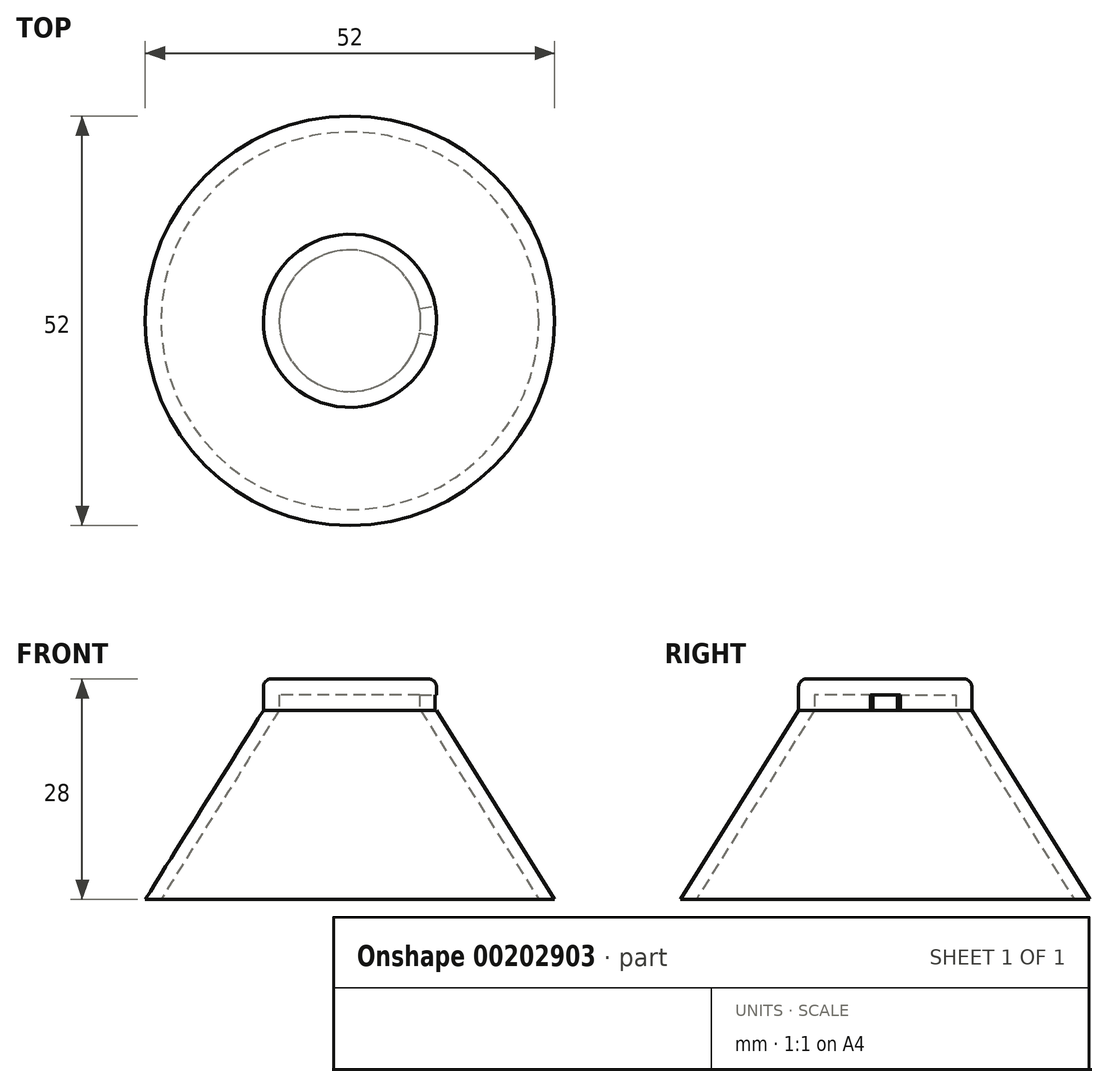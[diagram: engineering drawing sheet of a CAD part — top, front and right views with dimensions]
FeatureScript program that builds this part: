
annotation { "Feature Type Name" : "Feature", "Feature Type Description" : "" }
export const myFeature = defineFeature(function(context is Context, id is Id, definition is map)
    precondition{}
    {
        {
            var Q0;
            Q0=qCreatedBy(makeId("Front.planeOp"),FACE);
            var sketch = newSketch(context, id + "F0", { "sketchPlane" : qUnion([Q0])});
            skLineSegment(sketch, "E0", {"start": v(9, 24) * mm, "end": v(24, 0) * mm});
            skLineSegment(sketch, "E1", {"start": v(9, 24) * mm, "end": v(11, 24) * mm});
            skLineSegment(sketch, "E2", {"start": v(11, 24) * mm, "end": v(26, 0) * mm});
            skLineSegment(sketch, "E3", {"start": v(26, 0) * mm, "end": v(24, 0) * mm});
            skLineSegment(sketch, "E4", {"start": v(0, 0) * mm, "end": v(0, 24) * mm, "construction": true});
            skSolve(sketch);
        }
        {
            var Q0;
            Q0=qSketchRegion(id+"F0",true);
            var Q1;
            Q1=sQuery(id+"F0.wireOp",EDGE,"E4");
            revolve(context, id + "F1", {"entities" : qUnion([Q0]), "axis" : qUnion([Q1]), "revolveType" : RevolveType.FULL});
        }
        {
            var Q0;
            Q0=qCreatedBy(makeId("Front.planeOp"),FACE);
            var sketch = newSketch(context, id + "F2", { "sketchPlane" : qUnion([Q0])});
            skLineSegment(sketch, "E5", {"start": v(0, 0) * mm, "end": v(0, 57.6) * mm, "construction": true});
            skLineSegment(sketch, "E6", {"start": v(9, 24) * mm, "end": v(0, 38.46) * mm, "construction": true});
            skSolve(sketch);
        }
        {
            var Q0;
            Q0=makeQuery(id+"F1.opRevolve","SWEPT_FACE",FACE,{"disambiguationData":[OSD([sQuery(id+"F0.wireOp",EDGE,"E1")])]});
            extrude(context, id + "F3", {"entities" : qUnion([Q0]), "depth" : 2 * mm});
        }
        {
            var Q0;
            Q0=qCreatedBy(makeId("Front.planeOp"),FACE);
            var sketch = newSketch(context, id + "F4", { "sketchPlane" : qUnion([Q0])});
            skLineSegment(sketch, "E7.bottom", {"start": v(9, 26) * mm, "end": v(11, 26) * mm});
            skLineSegment(sketch, "E7.top", {"start": v(9, 24) * mm, "end": v(11, 24) * mm});
            skLineSegment(sketch, "E7.left", {"start": v(9, 26) * mm, "end": v(9, 24) * mm});
            skLineSegment(sketch, "E7.right", {"start": v(11, 26) * mm, "end": v(11, 24) * mm});
            skSolve(sketch);
        }
        {
            var Q0;
            {var subQ0=sQuery(id+"F0.wireOp",EDGE,"E1");var subQ3=sQuery(id+"F4.wireOp",EDGE,"E7.right");var subQ4=sQuery(id+"F4.wireOp",EDGE,"E7.left");var subQ5=sQuery(id+"F4.wireOp",EDGE,"E7.top");var subQ6=sQuery(id+"F4.wireOp",EDGE,"E7.bottom");var subQ7=makeQuery(id+"FlPVtqmiziweMUE_2.4.F7.opRevolve","CAP_FACE",FACE,{"disambiguationData":[OSD([subQ6,subQ5,subQ4,subQ3])],"isStart":true});var subQ8=makeQuery(id+"F7.boolean.opBoolean","COPY",FACE,{"derivedFrom":makeQuery(id+"F7.opRevolve","CAP_FACE",FACE,{"disambiguationData":[OSD([subQ6,subQ5,subQ4,subQ3])],"isStart":false})});Q0=makeQuery(id+"FlPVtqmiziweMUE_2.5.F7.boolean.opBoolean","SPLIT",FACE,{"disambiguationData":[TD([makeQuery(id+"FlPVtqmiziweMUE_2.4.F7.boolean.opBoolean","COPY",FACE,{"derivedFrom":subQ7})])],"derivedFrom":makeQuery(id+"FlPVtqmiziweMUE_2.4.F7.boolean.opBoolean","SPLIT",FACE,{"disambiguationData":[TD([subQ8])],"derivedFrom":makeQuery(id+"FlPVtqmiziweMUE_2.3.F7.boolean.opBoolean","SPLIT",FACE,{"disambiguationData":[TD([subQ8])],"derivedFrom":makeQuery(id+"FlPVtqmiziweMUE_2.2.F7.boolean.opBoolean","SPLIT",FACE,{"disambiguationData":[TD([subQ8])],"derivedFrom":makeQuery(id+"FlPVtqmiziweMUE_2.1.F7.boolean.opBoolean","SPLIT",FACE,{"disambiguationData":[TD([subQ8])],"derivedFrom":makeQuery(id+"F3.opExtrude","CAP_FACE",FACE,{"disambiguationData":[OSD([subQ0])],"isStart":false})})})})})});}
            var sketch = newSketch(context, id + "F5", { "sketchPlane" : qUnion([Q0])});
            skCircle(sketch, "E8", {"center": v(0, 0) * mm, "radius": 11 * mm});
            skSolve(sketch);
        }
        {
            var Q0;
            Q0 = qSketchRegion(id + "F5", true);
            extrude(context, id + "F6", {"entities" : qUnion([Q0]), "operationType" : NewBodyOperationType.ADD, "depth" : 2 * mm});
        }
        {
            var Q0;
            Q0 = qSketchRegion(id + "F4", true);
            var Q1;
            Q1=sQuery(id+"F2.wireOp",EDGE,"E5");
            revolve(context, id + "F7", {"operationType" : NewBodyOperationType.REMOVE, "entities" : qUnion([Q0]), "axis" : qUnion([Q1]), "revolveType" : RevolveType.TWO_DIRECTIONS, "oppositeDirection" : true, "angle" : 10 * degree, "angleBack" : 350 * degree});
        }
        {
            var Q0;
            Q0=makeQuery(id+"F6.opExtrude","CAP_EDGE",EDGE,{"disambiguationData":[OSD([sQuery(id+"F5.wireOp",EDGE,"E8")])],"isStart":false});
            fillet(context, id + "F8", {"entities" : qUnion([Q0]), "radius" : 1 * mm, "tangentPropagation" : true, "allowEdgeOverflow" : false});
        }
    });
